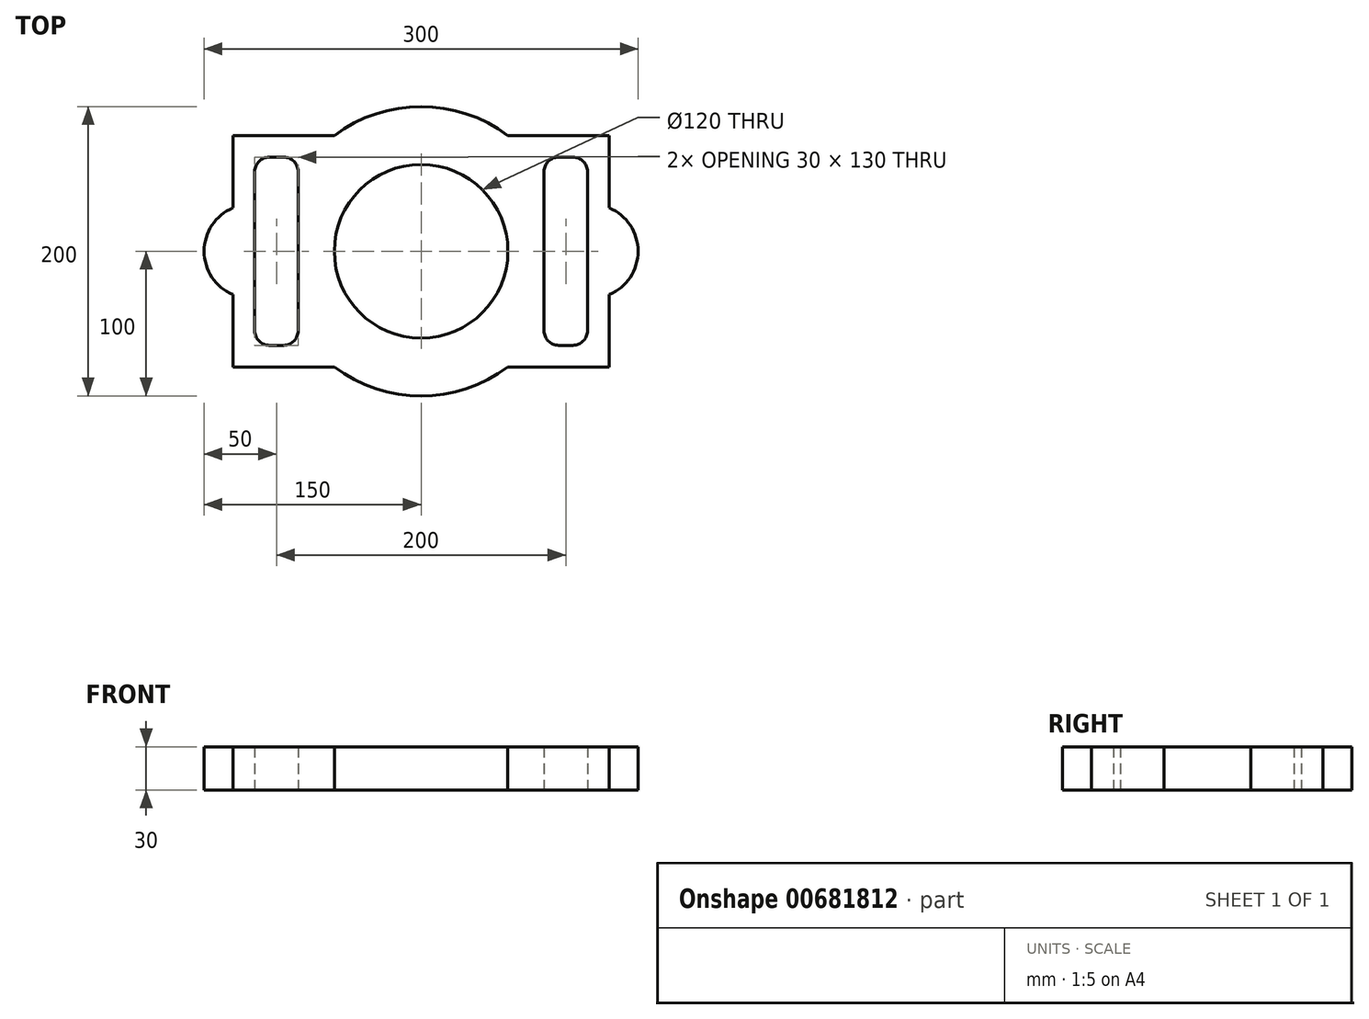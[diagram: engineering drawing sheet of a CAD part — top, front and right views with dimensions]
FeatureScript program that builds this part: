
annotation { "Feature Type Name" : "Feature", "Feature Type Description" : "" }
export const myFeature = defineFeature(function(context is Context, id is Id, definition is map)
    precondition{}
    {
        {
            var Q0;
            Q0=qCreatedBy(makeId("Top.planeOp"),FACE);
            var sketch = newSketch(context, id + "F0", { "sketchPlane" : qUnion([Q0])});
            skCircle(sketch, "E0", {"center": v(0, 0) * mm, "radius": 60 * mm});
            skArc(sketch, "E1", {"start": v(-60, -80) * mm, "mid": v(0, -100) * mm, "end": v(60, -80) * mm});
            skLineSegment(sketch, "E2", {"start": v(-60, 80) * mm, "end": v(-130, 80) * mm});
            skLineSegment(sketch, "E3", {"start": v(-130, 80) * mm, "end": v(-130, 30) * mm});
            skLineSegment(sketch, "E4", {"start": v(-130, -80) * mm, "end": v(-60, -80) * mm});
            skLineSegment(sketch, "E5", {"start": v(60, 80) * mm, "end": v(130, 80) * mm});
            skLineSegment(sketch, "E6", {"start": v(130, 80) * mm, "end": v(130, 30) * mm});
            skLineSegment(sketch, "E7", {"start": v(130, -80) * mm, "end": v(60, -80) * mm});
            skArc(sketch, "E8.trimOffspring", {"start": v(60, 80) * mm, "mid": v(0, 100) * mm, "end": v(-60, 80) * mm});
            skArc(sketch, "E9", {"start": v(-130, 30) * mm, "mid": v(-150, 0) * mm, "end": v(-130, -30) * mm});
            skArc(sketch, "E10", {"start": v(130, -30) * mm, "mid": v(150, 0) * mm, "end": v(130, 30) * mm});
            skPoint(sketch, "E10.startSnap0", {"position": v(130, 0) * mm});
            skLineSegment(sketch, "E11.trimOffspring", {"start": v(-130, -30) * mm, "end": v(-130, -80) * mm});
            skLineSegment(sketch, "E12.trimOffspring", {"start": v(130, -30) * mm, "end": v(130, -80) * mm});
            skLineSegment(sketch, "E13", {"start": v(-115, 55) * mm, "end": v(-115, -55) * mm});
            skLineSegment(sketch, "E14", {"start": v(-105, 65) * mm, "end": v(-95, 65) * mm});
            skLineSegment(sketch, "E15", {"start": v(-85, 55) * mm, "end": v(-85, -55) * mm});
            skLineSegment(sketch, "E16", {"start": v(-95, -65) * mm, "end": v(-105, -65) * mm});
            skLineSegment(sketch, "E17", {"start": v(95, 65) * mm, "end": v(105, 65) * mm});
            skLineSegment(sketch, "E18", {"start": v(115, 55) * mm, "end": v(115, -55) * mm});
            skLineSegment(sketch, "E19", {"start": v(85, 55) * mm, "end": v(85, -55) * mm});
            skLineSegment(sketch, "E20", {"start": v(95, -65) * mm, "end": v(105, -65) * mm});
            skPoint(sketch, "E21.visualSharp", {"position": v(-115, 65) * mm});
            skArc(sketch, "E21.filletArc", {"start": v(-105, 65) * mm, "mid": v(-112.07, 62.07) * mm, "end": v(-115, 55) * mm});
            skPoint(sketch, "E22.visualSharp", {"position": v(-85, 65) * mm});
            skArc(sketch, "E22.filletArc", {"start": v(-85, 55) * mm, "mid": v(-87.93, 62.07) * mm, "end": v(-95, 65) * mm});
            skPoint(sketch, "E23.visualSharp", {"position": v(-115, -65) * mm});
            skArc(sketch, "E23.filletArc", {"start": v(-115, -55) * mm, "mid": v(-112.07, -62.07) * mm, "end": v(-105, -65) * mm});
            skPoint(sketch, "E24.visualSharp", {"position": v(-85, -65) * mm});
            skArc(sketch, "E24.filletArc", {"start": v(-95, -65) * mm, "mid": v(-87.93, -62.07) * mm, "end": v(-85, -55) * mm});
            skPoint(sketch, "E25.visualSharp", {"position": v(85, -65) * mm});
            skArc(sketch, "E25.filletArc", {"start": v(85, -55) * mm, "mid": v(87.93, -62.07) * mm, "end": v(95, -65) * mm});
            skPoint(sketch, "E26.visualSharp", {"position": v(115, -65) * mm});
            skArc(sketch, "E26.filletArc", {"start": v(105, -65) * mm, "mid": v(112.07, -62.07) * mm, "end": v(115, -55) * mm});
            skPoint(sketch, "E27.visualSharp", {"position": v(85, 65) * mm});
            skArc(sketch, "E27.filletArc", {"start": v(95, 65) * mm, "mid": v(87.93, 62.07) * mm, "end": v(85, 55) * mm});
            skPoint(sketch, "E28.visualSharp", {"position": v(115, 65) * mm});
            skArc(sketch, "E28.filletArc", {"start": v(115, 55) * mm, "mid": v(112.07, 62.07) * mm, "end": v(105, 65) * mm});
            skSolve(sketch);
        }
        {
            var Q0;
            Q0=makeQuery(id+"F0.imprint","IMPRINT",FACE,{"disambiguationData":[TD([[makeQuery(id+"F0.imprint","IMPRINT",EDGE,{"derivedFrom":sQuery(id+"F0.wireOp",EDGE,"E0")}),-1.0]])]});
            extrude(context, id + "F1", {"entities" : qUnion([Q0]), "depth" : 30 * mm, "offsetDistance" : 25 * mm});
        }
    });
